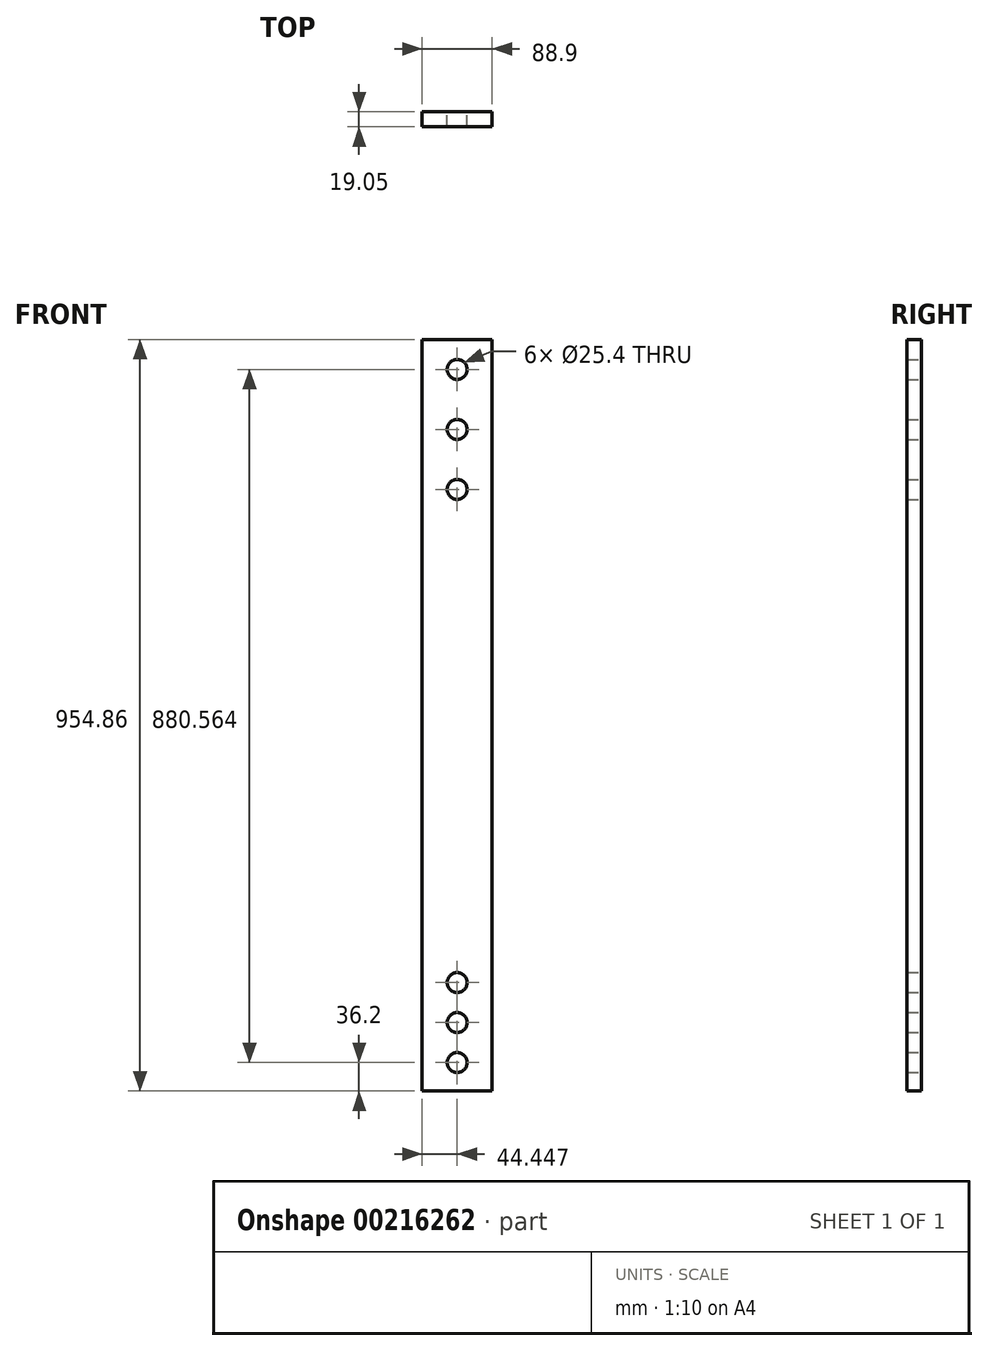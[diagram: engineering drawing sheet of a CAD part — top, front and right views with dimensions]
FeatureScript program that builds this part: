
annotation { "Feature Type Name" : "Feature", "Feature Type Description" : "" }
export const myFeature = defineFeature(function(context is Context, id is Id, definition is map)
    precondition{}
    {
        {
            var Q0;
            Q0=qCreatedBy(makeId("Front.planeOp"),FACE);
            var sketch = newSketch(context, id + "F0", { "sketchPlane" : qUnion([Q0])});
            skLineSegment(sketch, "E0", {"start": v(-1939.28, -1755.55) * mm, "end": v(-1850.38, -1755.55) * mm});
            skLineSegment(sketch, "E1", {"start": v(-1850.38, -1755.55) * mm, "end": v(-1850.38, -800.69) * mm});
            skLineSegment(sketch, "E2", {"start": v(-1850.38, -800.69) * mm, "end": v(-1939.28, -800.69) * mm});
            skLineSegment(sketch, "E3", {"start": v(-1939.28, -800.69) * mm, "end": v(-1939.28, -1755.55) * mm});
            skCircle(sketch, "E4", {"center": v(-1894.83, -838.79) * mm, "radius": 12.7 * mm});
            skCircle(sketch, "E5", {"center": v(-1894.83, -914.99) * mm, "radius": 12.7 * mm});
            skCircle(sketch, "E6", {"center": v(-1894.83, -991.19) * mm, "radius": 12.7 * mm});
            skCircle(sketch, "E7", {"center": v(-1894.83, -1617.75) * mm, "radius": 12.7 * mm});
            skCircle(sketch, "E8", {"center": v(-1894.83, -1668.55) * mm, "radius": 12.7 * mm});
            skCircle(sketch, "E9", {"center": v(-1894.83, -1719.35) * mm, "radius": 12.7 * mm});
            skLineSegment(sketch, "E10", {"start": v(-1894.83, -1755.55) * mm, "end": v(-1894.83, -800.69) * mm, "construction": true});
            skSolve(sketch);
        }
        {
            var Q0;
            Q0=makeQuery(id+"F0.imprint","IMPRINT",FACE,{"disambiguationData":[TD([[makeQuery(id+"F0.imprint","IMPRINT",EDGE,{"derivedFrom":sQuery(id+"F0.wireOp",EDGE,"E0")}),1.0]])]});
            extrude(context, id + "F1", {"entities" : qUnion([Q0]), "depth" : 19.05 * mm});
        }
    });
